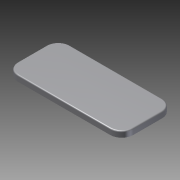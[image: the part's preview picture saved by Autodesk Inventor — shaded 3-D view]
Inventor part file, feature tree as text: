
AUTODESK INVENTOR PART (.ipt)
format: ipt  version: 2011 SP2 (Build 150309200, 309)  size: 95,744 bytes
history: native  units: mm
features: extrude x1, fillet x1, sketch x1
ambient origin geometry x8: Origin, YZ Plane, XZ Plane, XY Plane, X Axis, Y Axis, Z Axis, Center Point
bodies: Solid1 (feature_tree)
feature tree (3):
  extrude  "Extrusion1"  Depth=90.0mm
  fillet  "Fillet1"  Radius=45.0mm
  sketch  "Sketch1"  dims[d0=200.0mm d1=90.0mm d2=45.0mm d3=20.0mm d4=10.0mm d5=0.0mm d6=2.0mm]
